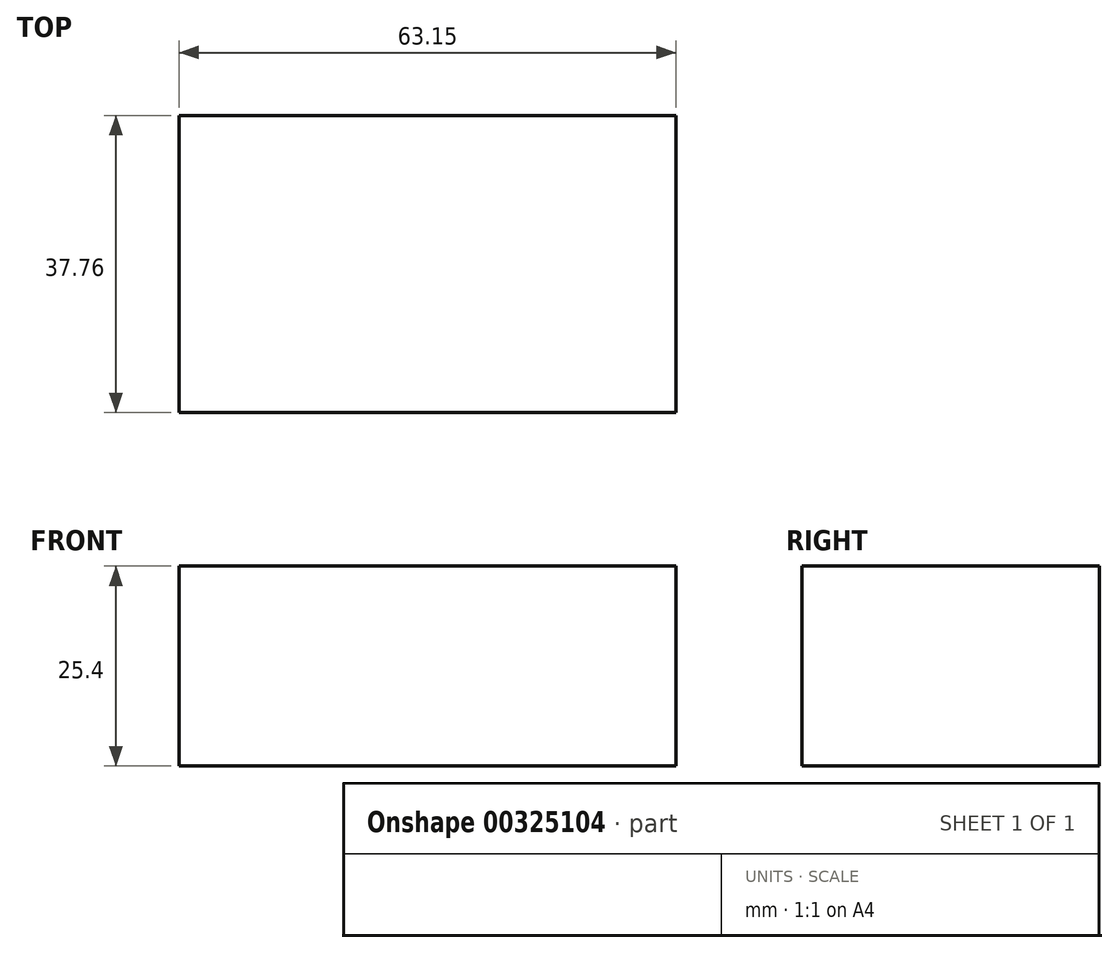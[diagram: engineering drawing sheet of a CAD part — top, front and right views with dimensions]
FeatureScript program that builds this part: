
annotation { "Feature Type Name" : "Feature", "Feature Type Description" : "" }
export const myFeature = defineFeature(function(context is Context, id is Id, definition is map)
    precondition{}
    {
        {
            var Q0;
            Q0=qCreatedBy(makeId("Top.planeOp"),FACE);
            var sketch = newSketch(context, id + "F0", { "sketchPlane" : qUnion([Q0])});
            skLineSegment(sketch, "E0.bottom", {"start": v(21.57, 66.1) * mm, "end": v(-41.58, 66.1) * mm});
            skLineSegment(sketch, "E0.top", {"start": v(21.57, 28.34) * mm, "end": v(-41.58, 28.34) * mm});
            skLineSegment(sketch, "E0.left", {"start": v(21.57, 66.1) * mm, "end": v(21.57, 28.34) * mm});
            skLineSegment(sketch, "E0.right", {"start": v(-41.58, 66.1) * mm, "end": v(-41.58, 28.34) * mm});
            skSolve(sketch);
        }
        {
            var Q0;
            Q0=makeQuery(id+"F0.imprint","IMPRINT",FACE,{"disambiguationData":[TD([[makeQuery(id+"F0.imprint","IMPRINT",EDGE,{"derivedFrom":sQuery(id+"F0.wireOp",EDGE,"E0.bottom")}),1.0]])]});
            extrude(context, id + "F1", {"entities" : qUnion([Q0]), "depth" : 25.4 * mm});
        }
    });
